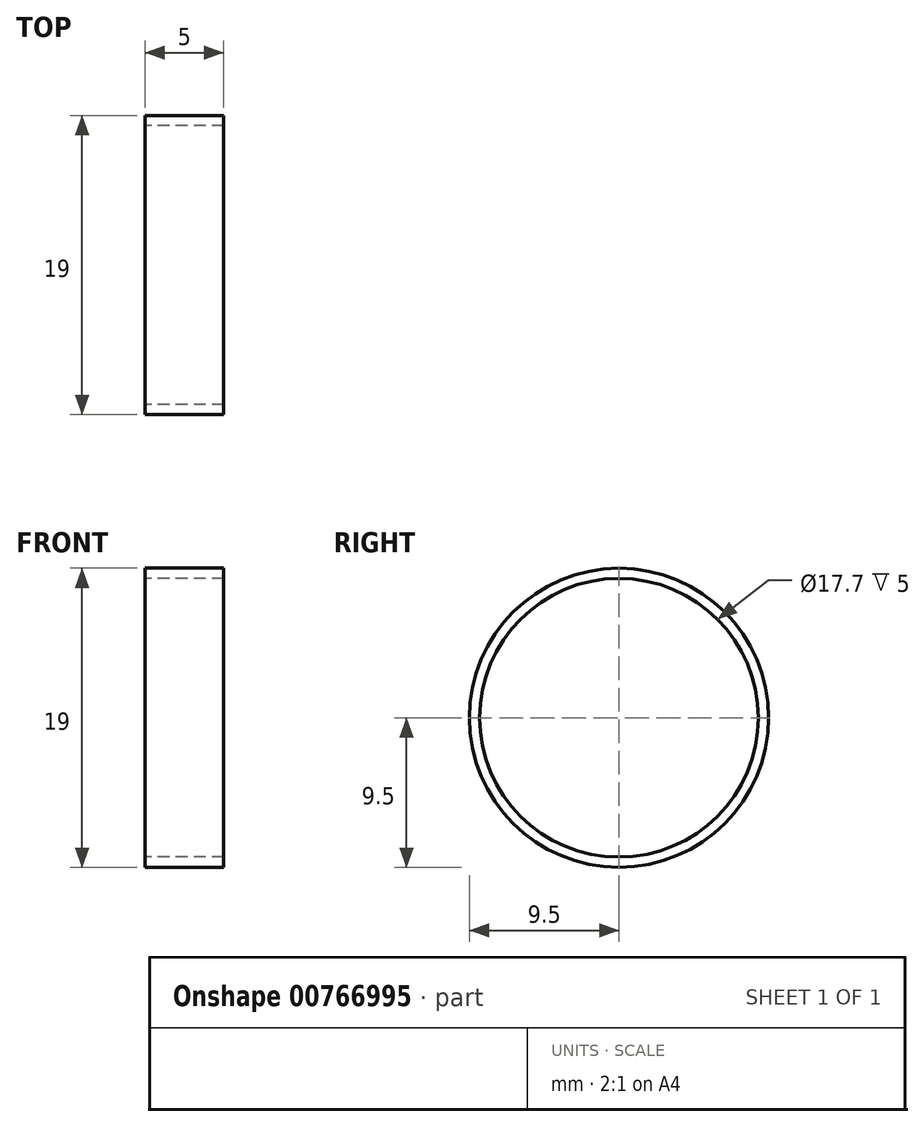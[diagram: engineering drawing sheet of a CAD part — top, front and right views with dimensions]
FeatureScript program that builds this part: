
annotation { "Feature Type Name" : "Feature", "Feature Type Description" : "" }
export const myFeature = defineFeature(function(context is Context, id is Id, definition is map)
    precondition{}
    {
        {
            var Q0;
            Q0=qCreatedBy(makeId("Right.planeOp"),FACE);
            var sketch = newSketch(context, id + "F0", { "sketchPlane" : qUnion([Q0])});
            skCircle(sketch, "E0", {"center": v(0, 0) * mm, "radius": 8.85 * mm});
            skCircle(sketch, "E1", {"center": v(0, 0) * mm, "radius": 9.5 * mm});
            skSolve(sketch);
        }
        {
            var Q0;
            Q0 = qSketchRegion(id + "F0", true);
            extrude(context, id + "F1", {"entities" : qUnion([Q0]), "depth" : 5 * mm, "offsetDistance" : 25.4 * mm});
        }
        {
            var Q0;
            Q0=qCreatedBy(makeId("Top.planeOp"),FACE);
            cPlane(context, id + "F2", {"entities" : qUnion([Q0]), "cplaneType" : CPlaneType.OFFSET, "offset" : (19 / 2) * mm, "width" : 152.4 * mm, "height" : 152.4 * mm});
        }
    });
